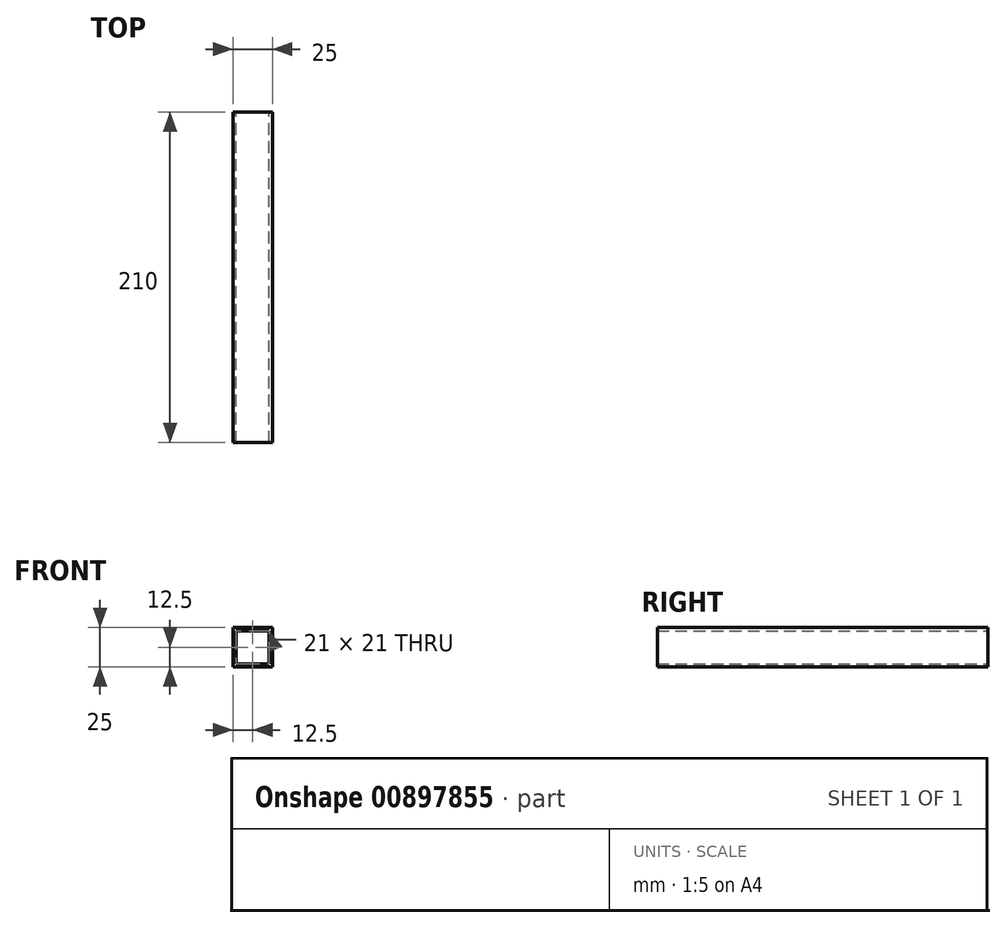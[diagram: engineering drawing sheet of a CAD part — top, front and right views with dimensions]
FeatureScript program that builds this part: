
annotation { "Feature Type Name" : "Feature", "Feature Type Description" : "" }
export const myFeature = defineFeature(function(context is Context, id is Id, definition is map)
    precondition{}
    {
        {
            var Q0;
            Q0=qCreatedBy(makeId("Front.planeOp"),FACE);
            var sketch = newSketch(context, id + "F0", { "sketchPlane" : qUnion([Q0])});
            skLineSegment(sketch, "E0.bottom", {"start": v(12.5, -12.5) * mm, "end": v(-12.5, -12.5) * mm});
            skLineSegment(sketch, "E0.top", {"start": v(12.5, 12.5) * mm, "end": v(-12.5, 12.5) * mm});
            skLineSegment(sketch, "E0.left", {"start": v(12.5, -12.5) * mm, "end": v(12.5, 12.5) * mm});
            skLineSegment(sketch, "E0.right", {"start": v(-12.5, -12.5) * mm, "end": v(-12.5, 12.5) * mm});
            skPoint(sketch, "E0.middle", {"position": v(0, 0) * mm});
            skLineSegment(sketch, "E1.0", {"start": v(10.5, 10.5) * mm, "end": v(-10.5, 10.5) * mm});
            skLineSegment(sketch, "E1.1", {"start": v(10.5, -10.5) * mm, "end": v(10.5, 10.5) * mm});
            skLineSegment(sketch, "E1.2", {"start": v(10.5, -10.5) * mm, "end": v(-10.5, -10.5) * mm});
            skLineSegment(sketch, "E1.3", {"start": v(-10.5, -10.5) * mm, "end": v(-10.5, 10.5) * mm});
            skSolve(sketch);
        }
        {
            var Q0;
            Q0=qSketchRegion(id+"F0",true);
            extrude(context, id + "F1", {"entities" : qUnion([Q0]), "depth" : 105 * mm, "offsetDistance" : 25 * mm, "hasSecondDirection" : true, "secondDirectionOppositeDirection" : true, "secondDirectionDepth" : 105 * mm});
        }
    });
